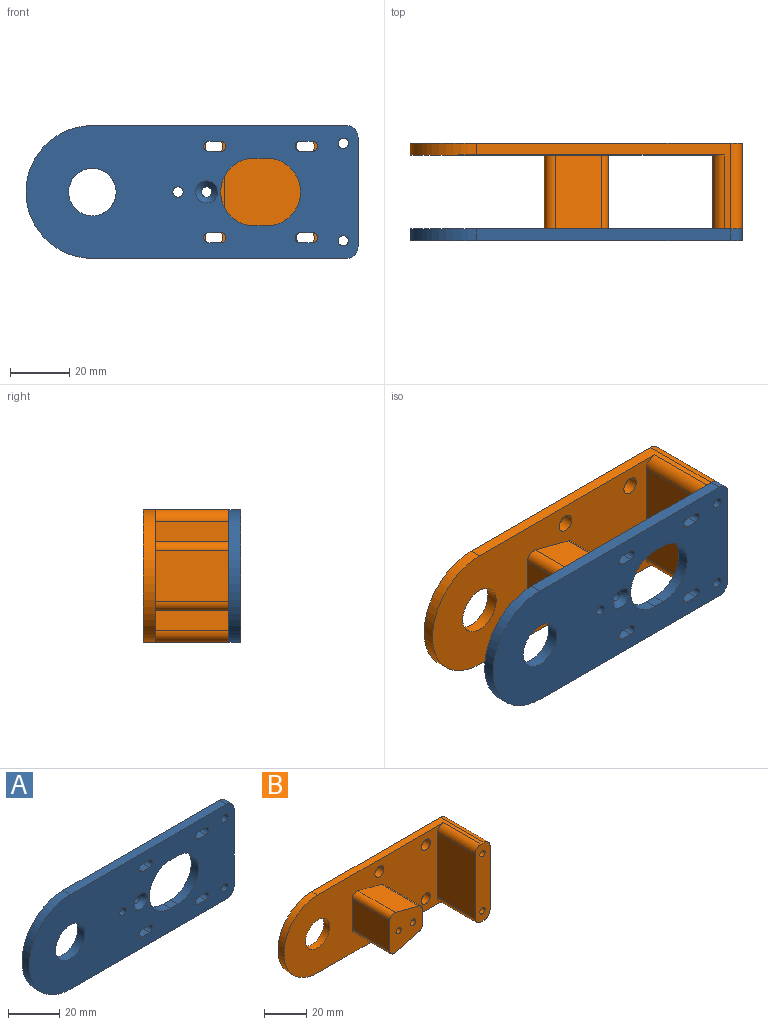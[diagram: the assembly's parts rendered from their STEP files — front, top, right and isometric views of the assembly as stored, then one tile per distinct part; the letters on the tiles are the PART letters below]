
ASSEMBLY  parts=2 mates=1
PART A: 34 faces, bbox 112.5x4x45 mm
  f0: plane 112.5x45mm, normal (0,-1,0), area 3959.8mm2, adj f2,f3,f4,f5,f6,f7,f8,f9
  f1: plane 112.5x45mm, normal (0,1,0), area 3994.3mm2, adj f2,f3,f4,f5,f6,f7,f8,f9
  f2: plane 37x4mm, normal (1,0,0), area 148mm2, adj f0,f1,f32,f33
  f3: plane 86x4mm, normal (0,0,1), area 344mm2, adj f0,f1,f4,f32
  f4: cylinder r=22.5mm len=45mm, axis (0,1,0), area 282.7mm2, adj f0,f1,f3,f5
  f5: plane 86x4mm, normal (0,0,-1), area 344mm2, adj f0,f1,f4,f33
  f6: plane 4x3.97mm, normal (0,0,1), area 15.9mm2, adj f0,f1,f7,f9
  f7: cylinder r=1.75mm len=4mm, axis (0,-1,0), area 22.3mm2, adj f0,f1,f6,f8
  f8: plane 4x3.96mm, normal (0,0,-1), area 15.8mm2, adj f0,f1,f7,f9
  f9: cylinder r=1.75mm len=4mm, axis (0,-1,0), area 22mm2, adj f0,f1,f6,f8
  f10: plane 4.03x4mm, normal (0,0,-1), area 16.1mm2, adj f0,f1,f11,f13
  f11: cylinder r=1.75mm len=4mm, axis (0,-1,0), area 22mm2, adj f0,f1,f10,f12
  f12: plane 4x3.96mm, normal (0,0,1), area 15.8mm2, adj f0,f1,f11,f13
  f13: cylinder r=1.75mm len=4mm, axis (0,-1,0), area 22mm2, adj f0,f1,f10,f12
  f14: plane 4.03x4mm, normal (0,0,-1), area 16.1mm2, adj f0,f1,f15,f17
  f15: cylinder r=1.75mm len=4mm, axis (0,-1,0), area 22mm2, adj f0,f1,f14,f16
  f16: plane 4x3.96mm, normal (0,0,1), area 15.8mm2, adj f0,f1,f15,f17
  f17: cylinder r=1.75mm len=4mm, axis (0,-1,0), area 22mm2, adj f0,f1,f14,f16
  f18: plane 4x4mm, normal (0,0,1), area 16mm2, adj f0,f1,f19,f21
  f19: cylinder r=11.5mm len=23mm, axis (0,-1,0), area 144.5mm2, adj f0,f1,f18,f20
  f20: plane 4x4mm, normal (0,0,-1), area 16mm2, adj f0,f1,f19,f21
  f21: cylinder r=11.5mm len=23mm, axis (0,-1,0), area 144.5mm2, adj f0,f1,f18,f20
  f22: plane 4.03x4mm, normal (0,0,1), area 16.1mm2, adj f0,f1,f23,f25
  f23: cylinder r=1.75mm len=4mm, axis (0,-1,0), area 22mm2, adj f0,f1,f22,f24
  f24: plane 4x3.96mm, normal (0,0,-1), area 15.8mm2, adj f0,f1,f23,f25
  f25: cylinder r=1.75mm len=4mm, axis (0,-1,0), area 22mm2, adj f0,f1,f22,f24
  f26: cylinder r=8.05mm len=16.1mm, axis (0,-1,0), area 202.3mm2, adj f0,f1
  f27: cylinder r=1.75mm len=4mm, axis (0,-1,0), area 44mm2, adj f0,f1
  f28: cylinder r=1.75mm len=3.5mm, axis (0,-1,0), area 22mm2, adj f1,f31
  f29: cylinder r=1.75mm len=4mm, axis (0,-1,0), area 44mm2, adj f0,f1
  f30: cylinder r=1.75mm len=4mm, axis (0,-1,0), area 44mm2, adj f0,f1
  f31: cone r=1.75mm half-angle=45deg, axis (0,-1,0), area 48.9mm2, adj f0,f28
  f32: cylinder r=4mm len=4mm, axis (0,1,0), area 25.1mm2, adj f0,f1,f2,f3
  f33: cylinder r=4mm len=4mm, axis (0,-1,0), area 25.1mm2, adj f0,f1,f2,f5
PART B: 30 faces, bbox 112.5x29x45 mm
  f0: plane 37x29mm, normal (1,0,0), area 1073mm2, adj f5,f13,f24,f25
  f1: plane 86x29mm, normal (0,0,1), area 394mm2, adj f2,f4,f5,f13,f22,f24
  f2: cylinder r=22.5mm len=45mm, axis (0,1,0), area 282.7mm2, adj f1,f3,f4,f5
  f3: plane 86x29mm, normal (0,0,-1), area 394mm2, adj f2,f4,f5,f13,f23,f25
  f4: plane 106.5x45mm, normal (0,-1,0), area 3671.6mm2, adj f1,f2,f3,f6,f7,f8,f9,f10
  f5: plane 112.5x45mm, normal (0,1,0), area 4483.2mm2, adj f0,f1,f2,f3,f6,f14,f15,f16
  f6: cylinder r=8.05mm len=16.1mm, axis (0,-1,0), area 202.3mm2, adj f4,f5
  f7: plane 25x15.7mm, normal (0.25,0,-0.97), area 405.7mm2, adj f4,f11,f18,f21
  f8: plane 25x9.17mm, normal (1,0,0), area 229.2mm2, adj f4,f11,f20,f21
  f9: plane 25x15.7mm, normal (0.25,0,0.97), area 405.7mm2, adj f4,f11,f19,f20
  f10: plane 25x17.38mm, normal (-1,0,0), area 434.6mm2, adj f4,f11,f18,f19
  f11: plane 23.38x21.7mm, normal (0,-1,0), area 394.5mm2, adj f7,f8,f9,f10,f14,f15,f18,f19
  f12: plane 37x25mm, normal (-1,0,0), area 925mm2, adj f4,f13,f22,f23
  f13: plane 45x10mm, normal (0,-1,0), area 417mm2, adj f0,f1,f3,f12,f16,f17,f22,f23
  f14: cylinder r=1.75mm len=29mm, axis (0,-1,0), area 318.9mm2, adj f5,f11
  f15: cylinder r=1.75mm len=29mm, axis (0,-1,0), area 318.9mm2, adj f5,f11
  f16: cylinder r=1.75mm len=29mm, axis (0,-1,0), area 318.9mm2, adj f5,f13
  f17: cylinder r=1.75mm len=29mm, axis (0,-1,0), area 318.9mm2, adj f5,f13
  f18: cylinder r=3mm len=25mm, axis (0,1,0), area 137mm2, adj f4,f7,f10,f11
  f19: cylinder r=3mm len=25mm, axis (0,-1,0), area 137mm2, adj f4,f9,f10,f11
  f20: cylinder r=3mm len=25mm, axis (0,-1,0), area 98.6mm2, adj f4,f8,f9,f11
  f21: cylinder r=3mm len=25mm, axis (0,1,0), area 98.6mm2, adj f4,f7,f8,f11
  f22: cylinder r=4mm len=25mm, axis (0,-1,0), area 157.1mm2, adj f1,f4,f12,f13
  f23: cylinder r=4mm len=25mm, axis (0,1,0), area 157.1mm2, adj f3,f4,f12,f13
  f24: cylinder r=4mm len=29mm, axis (0,1,0), area 182.2mm2, adj f0,f1,f5,f13
  f25: cylinder r=4mm len=29mm, axis (0,-1,0), area 182.2mm2, adj f0,f3,f5,f13
  f26: cylinder r=3mm len=6mm, axis (0,-1,0), area 75.4mm2, adj f4,f5
  f27: cylinder r=3mm len=6mm, axis (0,-1,0), area 75.4mm2, adj f4,f5
  f28: cylinder r=3mm len=6mm, axis (0,-1,0), area 75.4mm2, adj f4,f5
  f29: cylinder r=3mm len=6mm, axis (0,-1,0), area 75.4mm2, adj f4,f5
PLACE A t=(-21.68,-17.23,6.43)mm
PLACE B t=(-21.68,11.77,6.43)mm
MATE fastened B.f17 <-> A.f30  axis (0,-1,0) through (18.32,-17.23,22.93)mm
